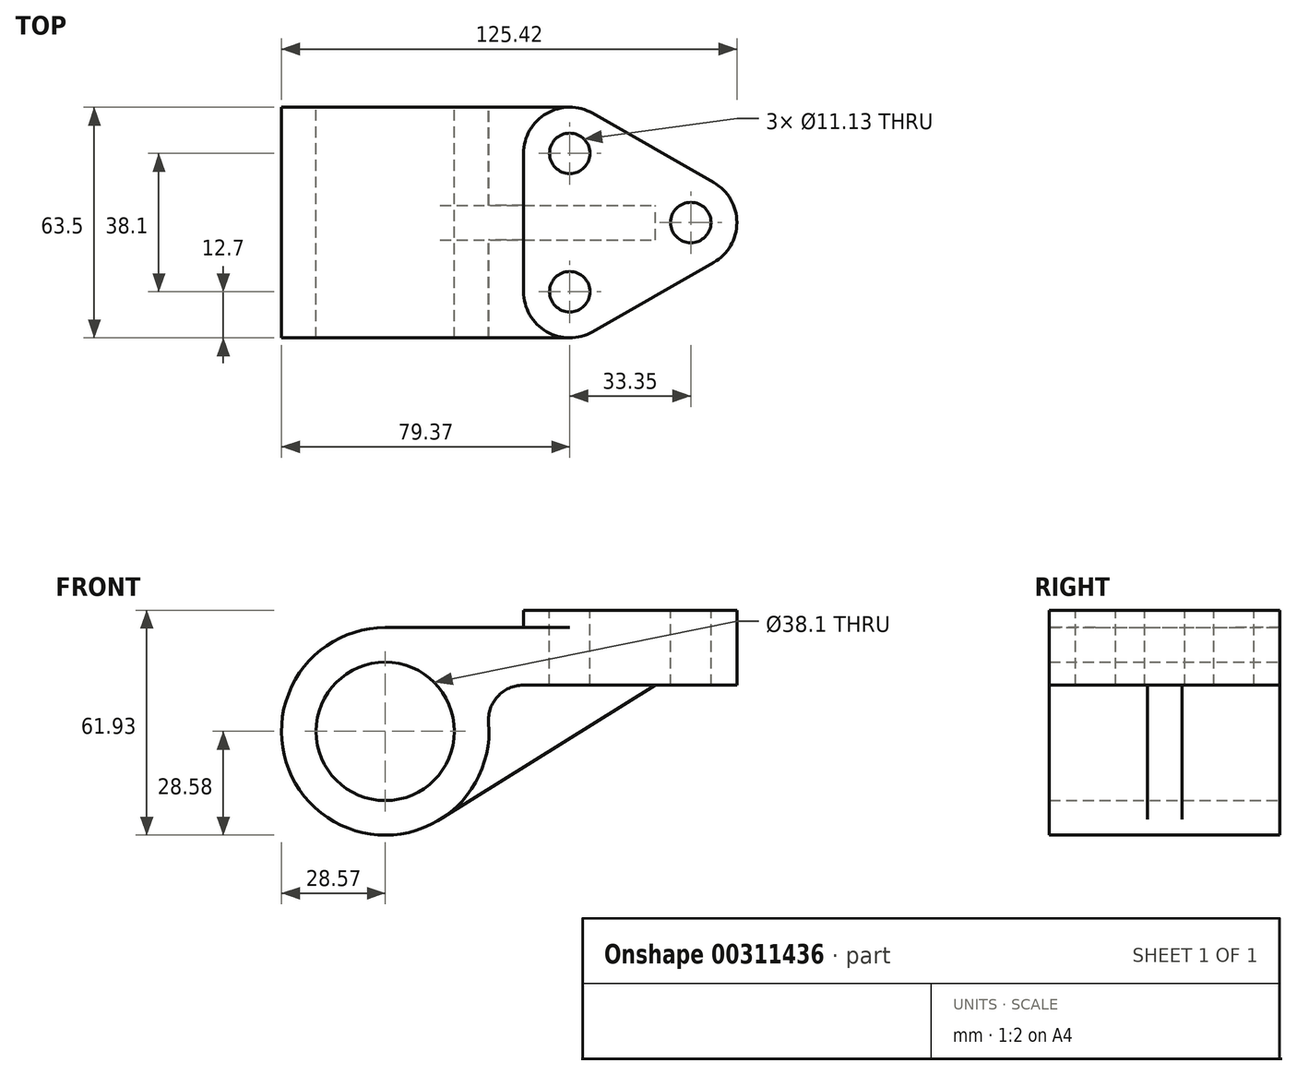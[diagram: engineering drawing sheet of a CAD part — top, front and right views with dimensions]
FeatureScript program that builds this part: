
annotation { "Feature Type Name" : "Feature", "Feature Type Description" : "" }
export const myFeature = defineFeature(function(context is Context, id is Id, definition is map)
    precondition{}
    {
        {
            var Q0;
            Q0=qCreatedBy(makeId("Front.planeOp"),FACE);
            var sketch = newSketch(context, id + "F0", { "sketchPlane" : qUnion([Q0])});
            skCircle(sketch, "E0", {"center": v(0, 0) * mm, "radius": 19.05 * mm});
            skArc(sketch, "E1", {"start": v(0, 28.58) * mm, "mid": v(-19.35, -21.03) * mm, "end": v(28.48, 2.38) * mm});
            skLineSegment(sketch, "E2", {"start": v(0, 28.58) * mm, "end": v(50.8, 28.58) * mm});
            skLineSegment(sketch, "E3", {"start": v(50.8, 28.58) * mm, "end": v(84.15, 28.58) * mm});
            skLineSegment(sketch, "E4", {"start": v(84.15, 28.58) * mm, "end": v(84.15, 12.7) * mm});
            skLineSegment(sketch, "E5", {"start": v(84.15, 12.7) * mm, "end": v(37.97, 12.7) * mm});
            skArc(sketch, "E6", {"start": v(37.97, 12.7) * mm, "mid": v(30.96, 9.62) * mm, "end": v(28.48, 2.38) * mm});
            skSolve(sketch);
        }
        {
            var Q0;
            Q0=makeQuery(id+"F0.imprint","IMPRINT",FACE,{"disambiguationData":[TD([[makeQuery(id+"F0.imprint","IMPRINT",EDGE,{"derivedFrom":sQuery(id+"F0.wireOp",EDGE,"E0")}),-1.0]])]});
            extrude(context, id + "F1", {"entities" : qUnion([Q0]), "endBound" : BoundingType.SYMMETRIC, "depth" : 63.5 * mm});
        }
        {
            var Q0;
            Q0=makeQuery(id+"F1.opExtrude","SWEPT_FACE",FACE,{"disambiguationData":[OSD([sQuery(id+"F0.wireOp",EDGE,"E2"),sQuery(id+"F0.wireOp",EDGE,"E3")])]});
            var sketch = newSketch(context, id + "F2", { "sketchPlane" : qUnion([Q0])});
            skLineSegment(sketch, "E7.0.0", {"start": v(84.15, 31.75) * mm, "end": v(0, 31.75) * mm});
            skLineSegment(sketch, "E7.0.1", {"start": v(0, 31.75) * mm, "end": v(0, -31.75) * mm});
            skLineSegment(sketch, "E7.0.2", {"start": v(0, -31.75) * mm, "end": v(84.15, -31.75) * mm});
            skLineSegment(sketch, "E7.0.3", {"start": v(84.15, -31.75) * mm, "end": v(84.15, 31.75) * mm});
            skLineSegment(sketch, "E8", {"start": v(0, 0) * mm, "end": v(84.15, 0) * mm, "construction": true});
            skLineSegment(sketch, "E9", {"start": v(50.8, 31.75) * mm, "end": v(50.8, -31.75) * mm, "construction": true});
            skArc(sketch, "E10", {"start": v(57.1, 30.08) * mm, "mid": v(44.42, 30.03) * mm, "end": v(38.1, 19.05) * mm});
            skArc(sketch, "E11", {"start": v(38.1, -19.05) * mm, "mid": v(44.42, -30.03) * mm, "end": v(57.1, -30.08) * mm});
            skArc(sketch, "E12", {"start": v(90.45, -11.03) * mm, "mid": v(96.85, 0) * mm, "end": v(90.45, 11.03) * mm});
            skLineSegment(sketch, "E13", {"start": v(90.45, -11.03) * mm, "end": v(57.1, -30.08) * mm});
            skLineSegment(sketch, "E14", {"start": v(90.45, 11.03) * mm, "end": v(57.1, 30.08) * mm});
            skLineSegment(sketch, "E15", {"start": v(38.1, -19.05) * mm, "end": v(38.1, 19.05) * mm});
            skSolve(sketch);
        }
        {
            var Q0;
            {var subQ0=sQuery(id+"F2.wireOp",EDGE,"E15");Q0=makeQuery(id+"F2.imprint","IMPRINT",FACE,{"disambiguationData":[TD([[makeQuery(id+"F2.imprint","IMPRINT",EDGE,{"derivedFrom":subQ0}),-1.0]])]});}
            var Q1;
            {var subQ5=sQuery(id+"F2.wireOp",EDGE,"E12");Q1=makeQuery(id+"F2.imprint","IMPRINT",FACE,{"disambiguationData":[TD([[makeQuery(id+"F2.imprint","IMPRINT",EDGE,{"derivedFrom":subQ5}),1.0]])]});}
            extrude(context, id + "F3", {"entities" : qUnion([Q0, Q1]), "operationType" : NewBodyOperationType.ADD, "depth" : 4.78 * mm});
        }
        {
            var Q0;
            {var subQ1=sQuery(id+"F2.wireOp",EDGE,"E13");var subQ3=sQuery(id+"F0.wireOp",EDGE,"E3");var subQ4=sQuery(id+"F0.wireOp",EDGE,"E2");var subQ5=makeQuery(id+"F1.opExtrude","SWEPT_FACE",FACE,{"disambiguationData":[OSD([subQ4,subQ3])]});Q0=makeQuery(id+"F3.boolean.opBoolean","SPLIT",FACE,{"disambiguationData":[TD([makeQuery(id+"F3.opExtrude","SWEPT_FACE",FACE,{"disambiguationData":[OSD([subQ1])]})])],"derivedFrom":subQ5});}
            var Q1;
            {var subQ2=sQuery(id+"F0.wireOp",EDGE,"E3");var subQ3=sQuery(id+"F0.wireOp",EDGE,"E2");var subQ4=makeQuery(id+"F1.opExtrude","SWEPT_FACE",FACE,{"disambiguationData":[OSD([subQ3,subQ2])]});var subQ5=sQuery(id+"F2.wireOp",EDGE,"E14");Q1=makeQuery(id+"F3.boolean.opBoolean","SPLIT",FACE,{"disambiguationData":[TD([makeQuery(id+"F3.opExtrude","SWEPT_FACE",FACE,{"disambiguationData":[OSD([subQ5])]})])],"derivedFrom":subQ4});}
            extrude(context, id + "F4", {"entities" : qUnion([Q0, Q1]), "operationType" : NewBodyOperationType.REMOVE, "oppositeDirection" : true, "depth" : 25.4 * mm});
        }
        {
            var Q0;
            Q0=makeQuery(id+"F3.opExtrude","CAP_FACE",FACE,{"disambiguationData":[OSD([sQuery(id+"F2.wireOp",EDGE,"E10"),sQuery(id+"F2.wireOp",EDGE,"E11"),sQuery(id+"F2.wireOp",EDGE,"E12"),sQuery(id+"F2.wireOp",EDGE,"E13"),sQuery(id+"F2.wireOp",EDGE,"E14"),sQuery(id+"F2.wireOp",EDGE,"E15")])],"isStart":true});
            extrude(context, id + "F5", {"entities" : qUnion([Q0]), "operationType" : NewBodyOperationType.ADD, "depth" : 15.88 * mm});
        }
        {
            var Q0;
            Q0=makeQuery(id+"F3.opExtrude","CAP_FACE",FACE,{"disambiguationData":[OSD([sQuery(id+"F2.wireOp",EDGE,"E10"),sQuery(id+"F2.wireOp",EDGE,"E11"),sQuery(id+"F2.wireOp",EDGE,"E12"),sQuery(id+"F2.wireOp",EDGE,"E13"),sQuery(id+"F2.wireOp",EDGE,"E14"),sQuery(id+"F2.wireOp",EDGE,"E15")])],"isStart":false});
            var sketch = newSketch(context, id + "F6", { "sketchPlane" : qUnion([Q0])});
            skLineSegment(sketch, "E16.0.0", {"start": v(57.1, -30.08) * mm, "end": v(90.45, -11.03) * mm});
            skArc(sketch, "E16.0.1", {"start": v(90.45, -11.03) * mm, "mid": v(96.85, 0) * mm, "end": v(90.45, 11.03) * mm});
            skLineSegment(sketch, "E16.0.2", {"start": v(90.45, 11.03) * mm, "end": v(57.1, 30.08) * mm});
            skArc(sketch, "E16.0.3", {"start": v(57.1, 30.08) * mm, "mid": v(44.42, 30.03) * mm, "end": v(38.1, 19.05) * mm});
            skLineSegment(sketch, "E16.0.4", {"start": v(38.1, 19.05) * mm, "end": v(38.1, -19.05) * mm});
            skArc(sketch, "E16.0.5", {"start": v(38.1, -19.05) * mm, "mid": v(44.42, -30.03) * mm, "end": v(57.1, -30.08) * mm});
            skCircle(sketch, "E17", {"center": v(50.8, 19.05) * mm, "radius": 5.56 * mm});
            skCircle(sketch, "E18", {"center": v(50.8, -19.05) * mm, "radius": 5.56 * mm});
            skCircle(sketch, "E19", {"center": v(84.15, 0) * mm, "radius": 5.56 * mm});
            skSolve(sketch);
        }
        {
            var Q0;
            Q0=makeQuery(id+"F6.imprint","IMPRINT",FACE,{"disambiguationData":[TD([[makeQuery(id+"F6.imprint","IMPRINT",EDGE,{"derivedFrom":sQuery(id+"F6.wireOp",EDGE,"E17")}),1.0]])]});
            var Q1;
            Q1=makeQuery(id+"F6.imprint","IMPRINT",FACE,{"disambiguationData":[TD([[makeQuery(id+"F6.imprint","IMPRINT",EDGE,{"derivedFrom":sQuery(id+"F6.wireOp",EDGE,"E18")}),1.0]])]});
            var Q2;
            Q2=makeQuery(id+"F6.imprint","IMPRINT",FACE,{"disambiguationData":[TD([[makeQuery(id+"F6.imprint","IMPRINT",EDGE,{"derivedFrom":sQuery(id+"F6.wireOp",EDGE,"E19")}),1.0]])]});
            extrude(context, id + "F7", {"entities" : qUnion([Q0, Q1, Q2]), "operationType" : NewBodyOperationType.REMOVE, "oppositeDirection" : true, "depth" : 25.4 * mm});
        }
        {
            var Q0;
            Q0=qCreatedBy(makeId("Front.planeOp"),FACE);
            var sketch = newSketch(context, id + "F8", { "sketchPlane" : qUnion([Q0])});
            skArc(sketch, "E20.0", {"start": v(0, 28.58) * mm, "mid": v(-19.35, -21.03) * mm, "end": v(28.48, 2.38) * mm});
            skLineSegment(sketch, "E21.0", {"start": v(57.1, 12.7) * mm, "end": v(90.45, 12.7) * mm});
            skLineSegment(sketch, "E22", {"start": v(15.12, -24.25) * mm, "end": v(74.4, 12.7) * mm});
            skLineSegment(sketch, "E23.0.0", {"start": v(37.97, 12.7) * mm, "end": v(50.8, 12.7) * mm});
            skLineSegment(sketch, "E23.0.1", {"start": v(50.8, 12.7) * mm, "end": v(50.8, 28.57) * mm});
            skLineSegment(sketch, "E23.0.2", {"start": v(50.8, 28.58) * mm, "end": v(0, 28.58) * mm});
            skArc(sketch, "E23.0.4", {"start": v(28.48, 2.38) * mm, "mid": v(30.96, 9.62) * mm, "end": v(37.97, 12.7) * mm});
            skLineSegment(sketch, "E24.0.1", {"start": v(90.45, 12.7) * mm, "end": v(90.45, 33.35) * mm});
            skLineSegment(sketch, "E24.0.2", {"start": v(90.45, 33.35) * mm, "end": v(57.1, 33.35) * mm});
            skLineSegment(sketch, "E24.0.3", {"start": v(57.1, 33.35) * mm, "end": v(57.1, 12.7) * mm});
            skLineSegment(sketch, "E25.0.0", {"start": v(38.1, 28.58) * mm, "end": v(50.8, 28.58) * mm});
            skLineSegment(sketch, "E25.0.1", {"start": v(50.8, 28.57) * mm, "end": v(50.8, 12.7) * mm});
            skLineSegment(sketch, "E25.0.2", {"start": v(50.8, 12.7) * mm, "end": v(57.1, 12.7) * mm});
            skLineSegment(sketch, "E25.0.3", {"start": v(57.1, 12.7) * mm, "end": v(57.1, 33.35) * mm});
            skLineSegment(sketch, "E25.0.4", {"start": v(57.1, 33.35) * mm, "end": v(38.1, 33.35) * mm});
            skLineSegment(sketch, "E25.0.5", {"start": v(38.1, 33.35) * mm, "end": v(38.1, 28.58) * mm});
            skSolve(sketch);
        }
        {
            var Q0;
            {var subQ1=sQuery(id+"F8.wireOp",EDGE,"E22");Q0=makeQuery(id+"F8.imprint","IMPRINT",FACE,{"disambiguationData":[TD([[makeQuery(id+"F8.imprint","IMPRINT",EDGE,{"derivedFrom":subQ1}),1.0]])]});}
            extrude(context, id + "F9", {"entities" : qUnion([Q0]), "operationType" : NewBodyOperationType.ADD, "endBound" : BoundingType.SYMMETRIC, "depth" : 9.52 * mm});
        }
    });
